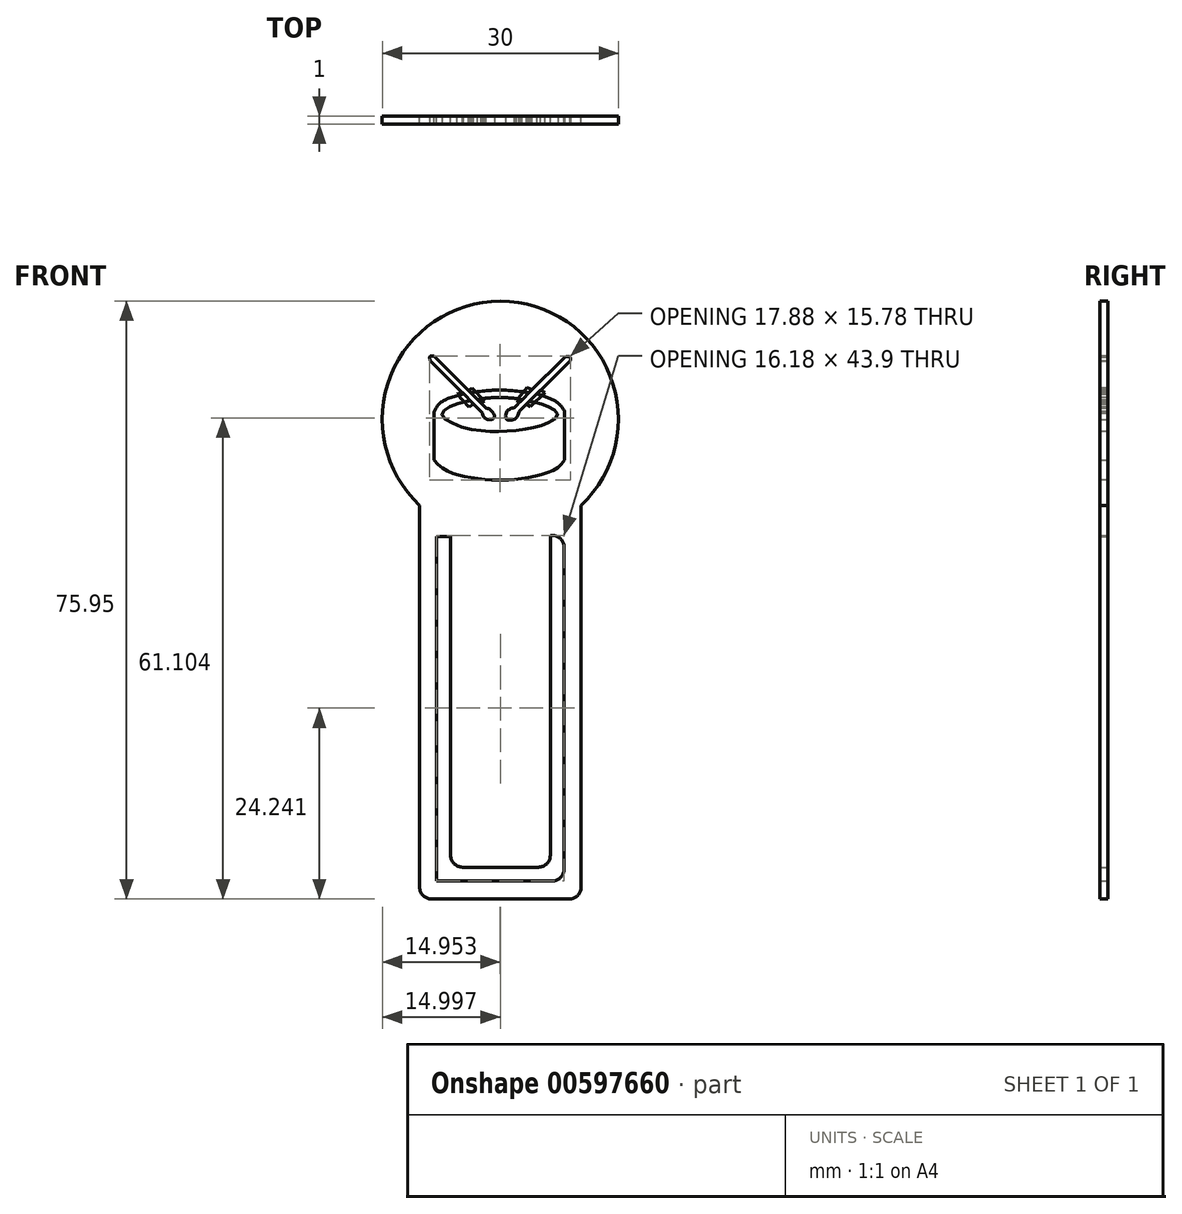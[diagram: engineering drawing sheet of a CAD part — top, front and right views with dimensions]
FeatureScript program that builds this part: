
annotation { "Feature Type Name" : "Feature", "Feature Type Description" : "" }
export const myFeature = defineFeature(function(context is Context, id is Id, definition is map)
    precondition{}
    {
        {
            var Q0;
            Q0=qCreatedBy(makeId("Front.planeOp"),FACE);
            var sketch = newSketch(context, id + "F0", { "sketchPlane" : qUnion([Q0])});
            skCircle(sketch, "E0", {"center": v(-22.83, 37.78) * mm, "radius": 15 * mm});
            skLineSegment(sketch, "E1.bottom", {"start": v(-33.08, 26.83) * mm, "end": v(-12.58, 26.83) * mm});
            skLineSegment(sketch, "E1.top", {"start": v(-33.08, -23.17) * mm, "end": v(-12.58, -23.17) * mm});
            skLineSegment(sketch, "E1.left", {"start": v(-33.08, 26.83) * mm, "end": v(-33.08, -23.17) * mm});
            skLineSegment(sketch, "E1.right", {"start": v(-12.58, 26.83) * mm, "end": v(-12.58, -23.17) * mm});
            skLineSegment(sketch, "E2.bottom", {"start": v(-66.52, 27.4) * mm, "end": v(-68.85, 27.4) * mm});
            skLineSegment(sketch, "E2.top", {"start": v(-66.52, 22.8) * mm, "end": v(-68.85, 22.8) * mm});
            skLineSegment(sketch, "E2.left", {"start": v(-68.85, 22.8) * mm, "end": v(-68.85, 27.4) * mm});
            skLineSegment(sketch, "E2.right", {"start": v(-66.52, 22.8) * mm, "end": v(-66.52, 27.4) * mm});
            skLineSegment(sketch, "E3.bottom", {"start": v(-66.52, 22.8) * mm, "end": v(-64.76, 22.8) * mm});
            skLineSegment(sketch, "E3.top", {"start": v(-66.52, 21.56) * mm, "end": v(-64.76, 21.56) * mm});
            skLineSegment(sketch, "E3.left", {"start": v(-66.52, 22.8) * mm, "end": v(-66.52, 21.56) * mm});
            skLineSegment(sketch, "E3.right", {"start": v(-64.76, 22.8) * mm, "end": v(-64.76, 21.56) * mm});
            skLineSegment(sketch, "E4.bottom", {"start": v(-30.92, 22.88) * mm, "end": v(-29.15, 22.88) * mm});
            skLineSegment(sketch, "E4.top", {"start": v(-30.92, -20.88) * mm, "end": v(-29.15, -20.88) * mm});
            skLineSegment(sketch, "E4.left", {"start": v(-30.92, 22.88) * mm, "end": v(-30.92, -20.88) * mm});
            skLineSegment(sketch, "E4.right", {"start": v(-29.15, 22.88) * mm, "end": v(-29.15, -20.88) * mm});
            skLineSegment(sketch, "E5.bottom", {"start": v(-30.92, -20.88) * mm, "end": v(-14.74, -20.88) * mm});
            skLineSegment(sketch, "E5.top", {"start": v(-30.92, -19.13) * mm, "end": v(-14.74, -19.13) * mm});
            skLineSegment(sketch, "E5.left", {"start": v(-30.92, -20.88) * mm, "end": v(-30.92, -19.13) * mm});
            skLineSegment(sketch, "E5.right", {"start": v(-14.74, -20.88) * mm, "end": v(-14.74, -19.13) * mm});
            skLineSegment(sketch, "E6.bottom", {"start": v(-14.74, -20.88) * mm, "end": v(-16.5, -20.88) * mm});
            skLineSegment(sketch, "E6.top", {"start": v(-14.74, 23.02) * mm, "end": v(-16.5, 23.02) * mm});
            skLineSegment(sketch, "E6.left", {"start": v(-14.74, -20.88) * mm, "end": v(-14.74, 23.02) * mm});
            skLineSegment(sketch, "E6.right", {"start": v(-16.5, -20.88) * mm, "end": v(-16.5, 23.02) * mm});
            skSolve(sketch);
        }
        {
            var Q0;
            {var subQ0=sQuery(id+"F0.wireOp",EDGE,"E1.bottom");var subQ1=sQuery(id+"F0.wireOp",EDGE,"E0");var subQ3=makeQuery(id+"F0.imprint","INTERSECT",VERTEX,{"derivedFrom":[subQ1,subQ0]});Q0=makeQuery(id+"F0.imprint","IMPRINT",FACE,{"disambiguationData":[TD([[makeQuery(id+"F0.imprint","IMPRINT",EDGE,{"disambiguationData":[TD([[subQ3,-1.0]])],"derivedFrom":subQ1}),1.0]])]});}
            var Q1;
            {var subQ0=sQuery(id+"F0.wireOp",EDGE,"E1.bottom");var subQ1=sQuery(id+"F0.wireOp",EDGE,"E0");var subQ3=makeQuery(id+"F0.imprint","INTERSECT",VERTEX,{"derivedFrom":[subQ1,subQ0]});Q1=makeQuery(id+"F0.imprint","IMPRINT",FACE,{"disambiguationData":[TD([[makeQuery(id+"F0.imprint","IMPRINT",EDGE,{"disambiguationData":[TD([[subQ3,1.0]])],"derivedFrom":subQ1}),1.0]])]});}
            var Q2;
            Q2=makeQuery(id+"F0.imprint","IMPRINT",FACE,{"disambiguationData":[TD([[makeQuery(id+"F0.imprint","IMPRINT",EDGE,{"derivedFrom":sQuery(id+"F0.wireOp",EDGE,"E1.top")}),1.0]])]});
            extrude(context, id + "F1", {"entities" : qUnion([Q0, Q1, Q2]), "depth" : 1 * mm, "offsetDistance" : 25 * mm});
        }
        {
            var Q0;
            Q0=makeQuery(id+"F1.opExtrude","SWEPT_EDGE",EDGE,{"disambiguationData":[OSD([sQuery(id+"F0.wireOp",EDGE,"E1.top"),sQuery(id+"F0.wireOp",EDGE,"E1.left")])]});
            var Q1;
            Q1=makeQuery(id+"F1.opExtrude","SWEPT_EDGE",EDGE,{"disambiguationData":[OSD([sQuery(id+"F0.wireOp",EDGE,"E4.right"),sQuery(id+"F0.wireOp",EDGE,"E5.top")])]});
            fillet(context, id + "F2", {"entities" : qUnion([Q0, Q1]), "radius" : 1.5 * mm, "tangentPropagation" : true, "allowEdgeOverflow" : false});
        }
        {
            var Q0;
            Q0=makeQuery(id+"F1.opExtrude","SWEPT_EDGE",EDGE,{"disambiguationData":[OSD([sQuery(id+"F0.wireOp",EDGE,"E1.top"),sQuery(id+"F0.wireOp",EDGE,"E1.right")])]});
            var Q1;
            Q1=makeQuery(id+"F1.opExtrude","SWEPT_EDGE",EDGE,{"disambiguationData":[OSD([sQuery(id+"F0.wireOp",EDGE,"E5.top"),sQuery(id+"F0.wireOp",EDGE,"E6.right")])]});
            fillet(context, id + "F3", {"entities" : qUnion([Q0, Q1]), "radius" : 1.5 * mm, "tangentPropagation" : true, "allowEdgeOverflow" : false});
        }
        {
            var Q0;
            Q0=makeQuery(id+"F1.opExtrude","SWEPT_EDGE",EDGE,{"disambiguationData":[OSD([sQuery(id+"F0.wireOp",EDGE,"E6.bottom"),sQuery(id+"F0.wireOp",EDGE,"E6.left")])]});
            fillet(context, id + "F4", {"entities" : qUnion([Q0]), "radius" : 1.5 * mm, "tangentPropagation" : true, "allowEdgeOverflow" : false});
        }
        {
            var Q0;
            Q0=makeQuery(id+"F1.opExtrude","SWEPT_EDGE",EDGE,{"disambiguationData":[OSD([sQuery(id+"F0.wireOp",EDGE,"E5.bottom"),sQuery(id+"F0.wireOp",EDGE,"E5.left")])]});
            fillet(context, id + "F5", {"entities" : qUnion([Q0]), "radius" : 1.5 * mm, "tangentPropagation" : true, "allowEdgeOverflow" : false});
        }
        {
            var Q0;
            Q0=qCreatedBy(makeId("Front.planeOp"),FACE);
            var sketch = newSketch(context, id + "F6", { "sketchPlane" : qUnion([Q0])});
            skLineSegment(sketch, "E7", {"start": v(-27.52, 40.97) * mm, "end": v(-31.77, 45.22) * mm});
            skFitSpline(sketch, "E8", {"points": [v(-31.77, 45.22) * mm, v(-31.77, 45.77) * mm, v(-31.25, 45.77) * mm], "startDerivative": vector(-0.27, 1.36) * mm, "endDerivative": vector(1.31, -0.27) * mm});
            skLineSegment(sketch, "E9", {"start": v(-31.25, 45.77) * mm, "end": v(-26.64, 41.17) * mm});
            skFitSpline(sketch, "E10", {"points": [v(-26.64, 41.17) * mm, v(-24.44, 41.4) * mm, v(-23, 41.49) * mm, v(-21.33, 41.4) * mm, v(-19.18, 41.17) * mm], "startDerivative": vector(8.54, 0.98) * mm, "endDerivative": vector(8.19, -1) * mm});
            skLineSegment(sketch, "E11", {"start": v(-19.18, 41.17) * mm, "end": v(-14.64, 45.69) * mm});
            skFitSpline(sketch, "E12", {"points": [v(-14.64, 45.69) * mm, v(-14, 45.69) * mm, v(-13.96, 45.18) * mm], "startDerivative": vector(1.49, 0.28) * mm, "endDerivative": vector(-0.16, -1.32) * mm});
            skLineSegment(sketch, "E13", {"start": v(-13.96, 45.18) * mm, "end": v(-18.17, 40.99) * mm});
            skFitSpline(sketch, "E14", {"points": [v(-18.17, 40.99) * mm, v(-16.73, 40.5) * mm, v(-15.45, 39.79) * mm, v(-14.7, 38.8) * mm], "startDerivative": vector(4.17, -1.3) * mm, "endDerivative": vector(2.06, -3.39) * mm});
            skLineSegment(sketch, "E15", {"start": v(-14.7, 38.8) * mm, "end": v(-14.7, 32.6) * mm});
            skFitSpline(sketch, "E16", {"points": [v(-14.7, 32.6) * mm, v(-15.46, 31.73) * mm, v(-16.86, 30.97) * mm, v(-18.75, 30.48) * mm, v(-21.1, 30.13) * mm, v(-22.7, 30.05) * mm, v(-24.38, 30.11) * mm, v(-26.78, 30.4) * mm, v(-28.53, 30.8) * mm, v(-30.07, 31.46) * mm, v(-31.27, 32.6) * mm], "startDerivative": vector(-8.3, -11.12) * mm, "endDerivative": vector(-11.54, 12.93) * mm});
            skLineSegment(sketch, "E17", {"start": v(-31.27, 32.6) * mm, "end": v(-31.27, 38.72) * mm});
            skFitSpline(sketch, "E18", {"points": [v(-31.27, 38.72) * mm, v(-30.87, 39.43) * mm, v(-29.87, 40.22) * mm, v(-27.52, 40.97) * mm], "startDerivative": vector(1.3, 2.88) * mm, "endDerivative": vector(5.93, 1.52) * mm});
            skLineSegment(sketch, "E19", {"start": v(-26.69, 40.14) * mm, "end": v(-25.1, 38.56) * mm});
            skFitSpline(sketch, "E20", {"points": [v(-25.1, 38.56) * mm, v(-24.97, 38.12) * mm, v(-24.57, 37.8) * mm, v(-24, 37.73) * mm, v(-23.6, 38.08) * mm, v(-23.76, 38.56) * mm, v(-24.2, 39.06) * mm, v(-24.65, 39.18) * mm], "startDerivative": vector(0.6, -3.5) * mm, "endDerivative": vector(-3.42, 0.35) * mm});
            skLineSegment(sketch, "E21", {"start": v(-24.65, 39.18) * mm, "end": v(-25.72, 40.25) * mm});
            skFitSpline(sketch, "E22", {"points": [v(-25.72, 40.25) * mm, v(-24.6, 40.45) * mm, v(-23, 40.53) * mm, v(-21.39, 40.47) * mm, v(-20.06, 40.25) * mm], "startDerivative": vector(4.73, 1.04) * mm, "endDerivative": vector(5.31, -1.06) * mm});
            skLineSegment(sketch, "E23", {"start": v(-20.06, 40.25) * mm, "end": v(-21.06, 39.26) * mm});
            skFitSpline(sketch, "E24", {"points": [v(-21.06, 39.26) * mm, v(-21.62, 39.08) * mm, v(-22.1, 38.54) * mm, v(-22.02, 37.75) * mm, v(-21.25, 37.71) * mm, v(-20.7, 38.12) * mm, v(-20.48, 38.77) * mm, v(-20.5, 38.77) * mm], "startDerivative": vector(-3.86, -0.8) * mm, "endDerivative": vector(-0.85, -0.36) * mm});
            skLineSegment(sketch, "E25", {"start": v(-20.48, 38.77) * mm, "end": v(-19.13, 40.06) * mm});
            skFitSpline(sketch, "E26", {"points": [v(-19.13, 40.06) * mm, v(-17.69, 39.74) * mm, v(-16.47, 39.27) * mm, v(-15.63, 38.58) * mm, v(-15.59, 38.16) * mm, v(-16.65, 37.37) * mm, v(-18.05, 36.87) * mm, v(-19.83, 36.5) * mm, v(-22.02, 36.25) * mm, v(-23.82, 36.23) * mm, v(-25.82, 36.38) * mm, v(-28.37, 37.02) * mm, v(-29.98, 37.93) * mm, v(-30.27, 38.43) * mm, v(-29.85, 38.97) * mm, v(-28.48, 39.68) * mm, v(-26.69, 40.14) * mm], "startDerivative": vector(23.32, -4.84) * mm, "endDerivative": vector(25.8, 5.39) * mm});
            skLineSegment(sketch, "E27", {"start": v(-27.52, 40.97) * mm, "end": v(-26.69, 40.14) * mm});
            skLineSegment(sketch, "E28", {"start": v(-26.64, 41.17) * mm, "end": v(-25.72, 40.25) * mm});
            skLineSegment(sketch, "E29", {"start": v(-19.18, 41.17) * mm, "end": v(-20.06, 40.25) * mm});
            skLineSegment(sketch, "E30", {"start": v(-18.17, 40.99) * mm, "end": v(-19.13, 40.06) * mm});
            skLineSegment(sketch, "E31", {"start": v(-20.84, 40.33) * mm, "end": v(-20.71, 40.43) * mm});
            skLineSegment(sketch, "E32", {"start": v(-28.1, 40.96) * mm, "end": v(-26.76, 39.61) * mm});
            skLineSegment(sketch, "E33", {"start": v(-26.25, 41.46) * mm, "end": v(-24.83, 39.95) * mm});
            skLineSegment(sketch, "E34", {"start": v(-19.42, 41.67) * mm, "end": v(-21.02, 39.9) * mm});
            skLineSegment(sketch, "E35", {"start": v(-18.9, 39.57) * mm, "end": v(-17.27, 41.24) * mm});
            skSolve(sketch);
        }
        {
            var Q0;
            Q0 = qSketchRegion(id + "F6", true);
            extrude(context, id + "F7", {"entities" : qUnion([Q0]), "operationType" : NewBodyOperationType.REMOVE, "depth" : 2 * mm, "offsetDistance" : 25 * mm, "hasSecondDirection" : true, "secondDirectionOppositeDirection" : true, "secondDirectionDepth" : 2 * mm});
        }
        {
            var Q0;
            Q0=qCreatedBy(makeId("Front.planeOp"),FACE);
            var sketch = newSketch(context, id + "F8", { "sketchPlane" : qUnion([Q0])});
            skLineSegment(sketch, "E36", {"start": v(-27.65, 41.14) * mm, "end": v(-26.24, 39.68) * mm});
            skLineSegment(sketch, "E37", {"start": v(-26.24, 39.68) * mm, "end": v(-26.83, 39.34) * mm});
            skLineSegment(sketch, "E38", {"start": v(-26.83, 39.34) * mm, "end": v(-28.36, 41) * mm});
            skLineSegment(sketch, "E39", {"start": v(-28.36, 41) * mm, "end": v(-27.65, 41.14) * mm});
            skLineSegment(sketch, "E40", {"start": v(-26.88, 41.41) * mm, "end": v(-25.3, 39.83) * mm});
            skLineSegment(sketch, "E41", {"start": v(-25.3, 39.83) * mm, "end": v(-24.84, 40.08) * mm});
            skLineSegment(sketch, "E42", {"start": v(-24.84, 40.08) * mm, "end": v(-26.46, 41.73) * mm});
            skLineSegment(sketch, "E43", {"start": v(-26.46, 41.73) * mm, "end": v(-26.88, 41.41) * mm});
            skLineSegment(sketch, "E44", {"start": v(-18.83, 41.54) * mm, "end": v(-20.33, 39.97) * mm});
            skLineSegment(sketch, "E45", {"start": v(-20.33, 39.97) * mm, "end": v(-20.8, 40.15) * mm});
            skLineSegment(sketch, "E46", {"start": v(-20.8, 40.15) * mm, "end": v(-19.46, 41.8) * mm});
            skLineSegment(sketch, "E47", {"start": v(-19.46, 41.8) * mm, "end": v(-18.83, 41.54) * mm});
            skLineSegment(sketch, "E48", {"start": v(-17.71, 41.47) * mm, "end": v(-19.51, 39.7) * mm});
            skLineSegment(sketch, "E49", {"start": v(-19.51, 39.7) * mm, "end": v(-18.98, 39.36) * mm});
            skLineSegment(sketch, "E50", {"start": v(-18.98, 39.36) * mm, "end": v(-17.17, 41.18) * mm});
            skLineSegment(sketch, "E51", {"start": v(-17.17, 41.18) * mm, "end": v(-17.71, 41.47) * mm});
            skSolve(sketch);
        }
        {
            var Q0;
            Q0 = qSketchRegion(id + "F8", true);
            extrude(context, id + "F9", {"entities" : qUnion([Q0]), "depth" : 1 * mm, "offsetDistance" : 25 * mm});
        }
    });
